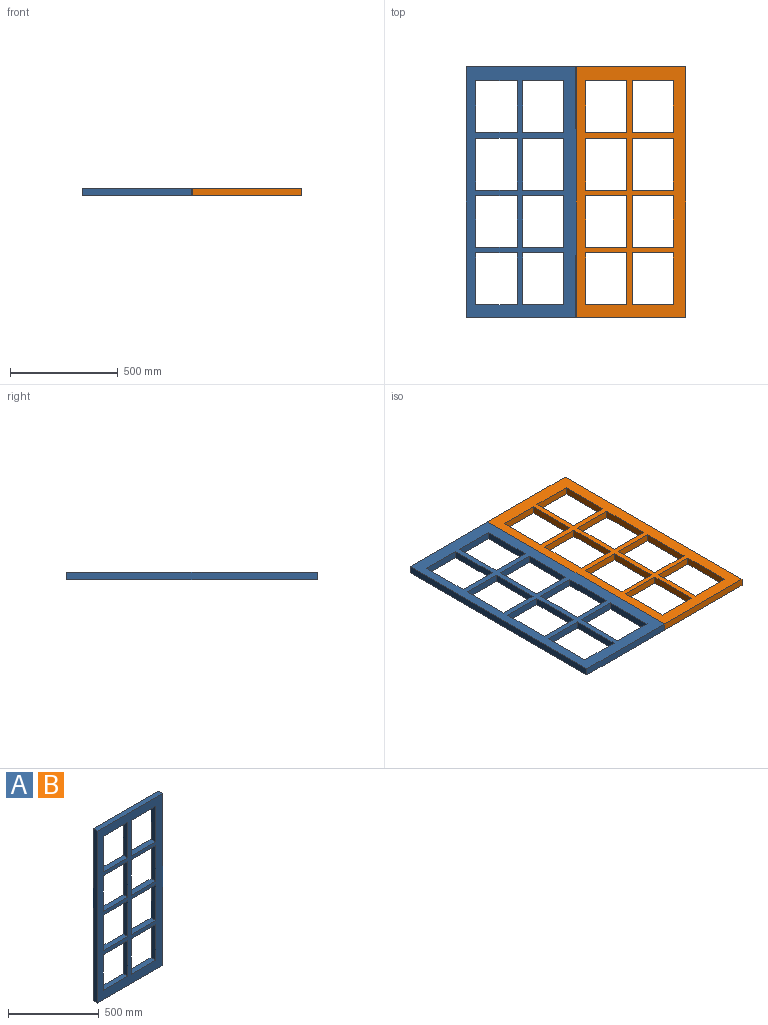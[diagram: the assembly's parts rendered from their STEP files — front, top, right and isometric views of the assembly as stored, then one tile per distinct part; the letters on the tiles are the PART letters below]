
ASSEMBLY  parts=2 mates=1
PART A: 38 faces, bbox 508x34.9x1158.9 mm
  f0: plane 240.03x34.93mm, normal (1,0,0), area 8383mm2, adj f1,f35,f36,f37
  f1: plane 190.5x34.93mm, normal (0,0,-1), area 6653.2mm2, adj f0,f2,f36,f37
  f2: plane 240.03x34.93mm, normal (-1,0,0), area 8383mm2, adj f1,f35,f36,f37
  f3: plane 240.03x34.93mm, normal (1,0,0), area 8383mm2, adj f4,f27,f36,f37
  f4: plane 190.5x34.93mm, normal (0,0,-1), area 6653.2mm2, adj f3,f5,f36,f37
  f5: plane 240.03x34.93mm, normal (-1,0,0), area 8383mm2, adj f4,f27,f36,f37
  f6: plane 240.03x34.93mm, normal (1,0,0), area 8383mm2, adj f7,f28,f36,f37
  f7: plane 190.5x34.93mm, normal (0,0,-1), area 6653.2mm2, adj f6,f8,f36,f37
  f8: plane 240.03x34.93mm, normal (-1,0,0), area 8383mm2, adj f7,f28,f36,f37
  f9: plane 508x34.93mm, normal (0,0,1), area 17741.9mm2, adj f10,f29,f36,f37
  f10: plane 1158.88x34.93mm, normal (-1,0,0), area 40473.7mm2, adj f9,f11,f36,f37
  f11: plane 508x34.93mm, normal (0,0,-1), area 17741.9mm2, adj f10,f29,f36,f37
  f12: plane 190.5x34.93mm, normal (0,0,1), area 6653.2mm2, adj f13,f30,f36,f37
  f13: plane 240.03x34.93mm, normal (1,0,0), area 8383mm2, adj f12,f14,f36,f37
  f14: plane 190.5x34.93mm, normal (0,0,-1), area 6653.2mm2, adj f13,f30,f36,f37
  f15: plane 190.5x34.93mm, normal (0,0,1), area 6653.2mm2, adj f16,f31,f36,f37
  f16: plane 240.03x34.93mm, normal (1,0,0), area 8383mm2, adj f15,f17,f36,f37
  f17: plane 190.5x34.93mm, normal (0,0,-1), area 6653.2mm2, adj f16,f31,f36,f37
  f18: plane 190.5x34.93mm, normal (0,0,1), area 6653.2mm2, adj f19,f32,f36,f37
  f19: plane 240.03x34.93mm, normal (1,0,0), area 8383mm2, adj f18,f20,f36,f37
  f20: plane 190.5x34.93mm, normal (0,0,-1), area 6653.2mm2, adj f19,f32,f36,f37
  f21: plane 190.5x34.93mm, normal (0,0,1), area 6653.2mm2, adj f22,f33,f36,f37
  f22: plane 240.03x34.93mm, normal (1,0,0), area 8383mm2, adj f21,f23,f36,f37
  f23: plane 190.5x34.93mm, normal (0,0,-1), area 6653.2mm2, adj f22,f33,f36,f37
  f24: plane 190.5x34.93mm, normal (0,0,1), area 6653.2mm2, adj f25,f34,f36,f37
  f25: plane 240.03x34.93mm, normal (1,0,0), area 8383mm2, adj f24,f26,f36,f37
  f26: plane 190.5x34.93mm, normal (0,0,-1), area 6653.2mm2, adj f25,f34,f36,f37
  f27: plane 190.5x34.93mm, normal (0,0,1), area 6653.2mm2, adj f3,f5,f36,f37
  f28: plane 190.5x34.93mm, normal (0,0,1), area 6653.2mm2, adj f6,f8,f36,f37
  f29: plane 1158.88x34.93mm, normal (1,0,0), area 40473.7mm2, adj f9,f11,f36,f37
  f30: plane 240.03x34.93mm, normal (-1,0,0), area 8383mm2, adj f12,f14,f36,f37
  f31: plane 240.03x34.93mm, normal (-1,0,0), area 8383mm2, adj f15,f17,f36,f37
  f32: plane 240.03x34.93mm, normal (-1,0,0), area 8383mm2, adj f18,f20,f36,f37
  f33: plane 240.03x34.93mm, normal (-1,0,0), area 8383mm2, adj f21,f23,f36,f37
  f34: plane 240.03x34.93mm, normal (-1,0,0), area 8383mm2, adj f24,f26,f36,f37
  f35: plane 190.5x34.93mm, normal (0,0,1), area 6653.2mm2, adj f0,f2,f36,f37
  f36: plane 1158.88x508mm, normal (0,-1,0), area 222902.8mm2, adj f0,f1,f2,f3,f4,f5,f6,f7
  f37: plane 1158.88x508mm, normal (0,1,0), area 222902.8mm2, adj f0,f1,f2,f3,f4,f5,f6,f7
PART B: same geometry as A
PLACE A rot(axis=(1,0,0),90deg) t=(-545.01,498.81,-191.47)mm
PLACE B rot(axis=(1,0,0),90deg) t=(-37.01,498.81,-191.47)mm
MATE fastened A.f29 <-> B.f10  axis (1,0,0) through (-37.01,-80.63,-208.93)mm
